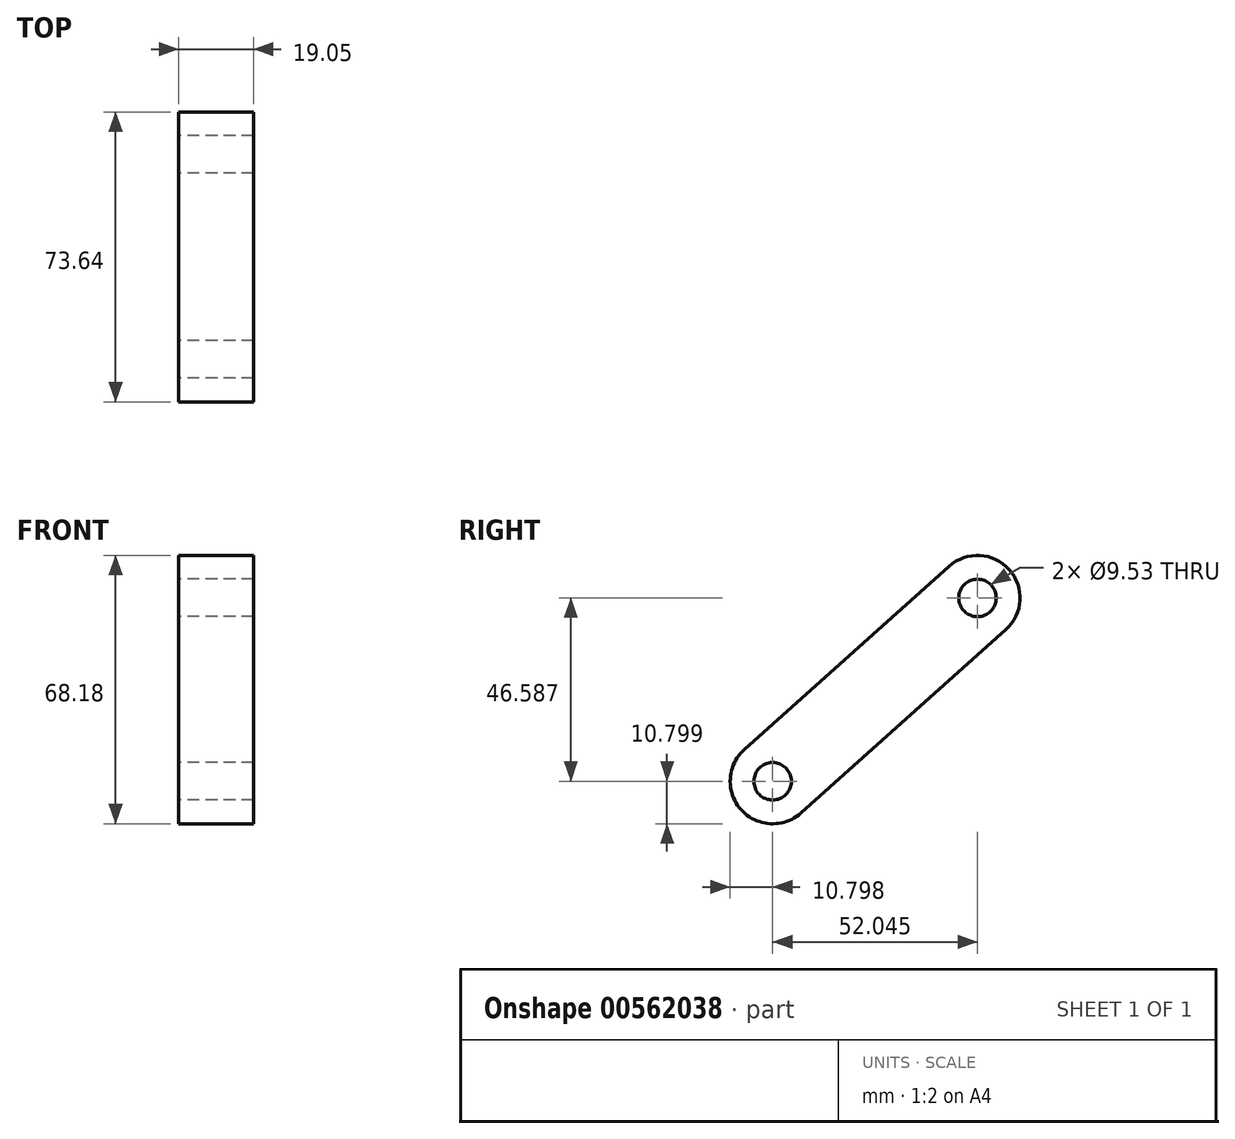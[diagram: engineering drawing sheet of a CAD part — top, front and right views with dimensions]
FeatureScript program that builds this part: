
annotation { "Feature Type Name" : "Feature", "Feature Type Description" : "" }
export const myFeature = defineFeature(function(context is Context, id is Id, definition is map)
    precondition{}
    {
        {
            var Q0;
            Q0=qCreatedBy(makeId("Right.planeOp"),FACE);
            var sketch = newSketch(context, id + "F0", { "sketchPlane" : qUnion([Q0])});
            skLineSegment(sketch, "E0", {"start": v(-513.86, 319.86) * mm, "end": v(-513.86, 78.56) * mm});
            skSolve(sketch);
        }
        {
            var Q0;
            Q0=qCreatedBy(makeId("Right.planeOp"),FACE);
            var sketch = newSketch(context, id + "F1", { "sketchPlane" : qUnion([Q0])});
            skLineSegment(sketch, "E1", {"start": v(-749.75, 255.82) * mm, "end": v(-601.81, 261.03) * mm});
            skLineSegment(sketch, "E2", {"start": v(-562.01, 653.81) * mm, "end": v(-601.81, 261.03) * mm});
            skLineSegment(sketch, "E3", {"start": v(-562.01, 653.81) * mm, "end": v(-749.75, 255.82) * mm});
            skLineSegment(sketch, "E4", {"start": v(-712.77, 291.22) * mm, "end": v(-724.6, 436.35) * mm});
            skLineSegment(sketch, "E5", {"start": v(-712.77, 291.22) * mm, "end": v(-827.72, 541.93) * mm});
            skLineSegment(sketch, "E6", {"start": v(-724.6, 436.35) * mm, "end": v(-827.72, 541.93) * mm});
            skLineSegment(sketch, "E7", {"start": v(-1010.22, 658.42) * mm, "end": v(-827.72, 541.93) * mm});
            skLineSegment(sketch, "E8", {"start": v(-1039.51, 675.34) * mm, "end": v(-1010.22, 658.42) * mm});
            skLineSegment(sketch, "E9", {"start": v(-1039.51, 675.34) * mm, "end": v(-712.77, 291.22) * mm});
            skLineSegment(sketch, "E10", {"start": v(-1010.22, 658.42) * mm, "end": v(-712.77, 291.22) * mm});
            skLineSegment(sketch, "E11", {"start": v(-601.81, 261.03) * mm, "end": v(-595.89, 401.8) * mm});
            skLineSegment(sketch, "E12", {"start": v(-601.81, 261.03) * mm, "end": v(-609.7, 655.84) * mm});
            skLineSegment(sketch, "E13", {"start": v(-595.89, 401.8) * mm, "end": v(-609.7, 655.84) * mm});
            skLineSegment(sketch, "E14", {"start": v(-724.6, 436.35) * mm, "end": v(-595.89, 401.8) * mm});
            skLineSegment(sketch, "E15", {"start": v(-827.72, 541.93) * mm, "end": v(-776.2, 589.57) * mm});
            skLineSegment(sketch, "E16", {"start": v(-749.75, 255.82) * mm, "end": v(-776.2, 589.57) * mm});
            skLineSegment(sketch, "E17", {"start": v(-1043.9, 791.38) * mm, "end": v(-776.2, 589.57) * mm});
            skLineSegment(sketch, "E18", {"start": v(-1392.46, 315.43) * mm, "end": v(-1338.48, 358.4) * mm});
            skLineSegment(sketch, "E19", {"start": v(-1338.48, 358.4) * mm, "end": v(-1296.78, 299.05) * mm});
            skLineSegment(sketch, "E20", {"start": v(-1043.9, 791.38) * mm, "end": v(-1296.78, 299.05) * mm});
            skLineSegment(sketch, "E21", {"start": v(-1296.78, 299.05) * mm, "end": v(-1039.51, 675.34) * mm});
            skLineSegment(sketch, "E22", {"start": v(-1039.51, 675.34) * mm, "end": v(-1043.9, 791.38) * mm});
            skLineSegment(sketch, "E23", {"start": v(-1010.22, 658.42) * mm, "end": v(-1338.48, 358.4) * mm});
            skLineSegment(sketch, "E24", {"start": v(-1392.46, 315.43) * mm, "end": v(-1296.78, 299.05) * mm});
            skLineSegment(sketch, "E25", {"start": v(-1296.78, 299.05) * mm, "end": v(-1296.78, 190.05) * mm});
            skLineSegment(sketch, "E26", {"start": v(-1296.78, 190.05) * mm, "end": v(-1404.89, 208.55) * mm});
            skLineSegment(sketch, "E27", {"start": v(-1404.89, 208.55) * mm, "end": v(-1392.46, 315.43) * mm});
            skLineSegment(sketch, "E28", {"start": v(-1392.46, 315.43) * mm, "end": v(-1296.78, 190.05) * mm});
            skLineSegment(sketch, "E29", {"start": v(0, 0) * mm, "end": v(0, 674.17) * mm});
            skLineSegment(sketch, "E30", {"start": v(-316.61, 320.6) * mm, "end": v(-316.61, 307.94) * mm});
            skLineSegment(sketch, "E31", {"start": v(-400.45, 218.07) * mm, "end": v(-378.01, 218.07) * mm});
            skLineSegment(sketch, "E32", {"start": v(-472.6, 74.76) * mm, "end": v(-472.6, 54.94) * mm});
            skSolve(sketch);
        }
        {
            var Q0;
            Q0=qCreatedBy(makeId("Right.planeOp"),FACE);
            var sketch = newSketch(context, id + "F2", { "sketchPlane" : qUnion([Q0])});
            skArc(sketch, "E33", {"start": v(-782.88, 596.56) * mm, "mid": v(-767.63, 595.72) * mm, "end": v(-768.48, 580.47) * mm});
            skArc(sketch, "E34", {"start": v(-834.92, 549.97) * mm, "mid": v(-835.76, 534.73) * mm, "end": v(-820.52, 533.89) * mm});
            skLineSegment(sketch, "E35", {"start": v(-834.92, 549.97) * mm, "end": v(-782.88, 596.56) * mm});
            skLineSegment(sketch, "E36", {"start": v(-768.48, 580.47) * mm, "end": v(-820.52, 533.89) * mm});
            skCircle(sketch, "E37", {"center": v(-775.68, 588.52) * mm, "radius": 4.76 * mm});
            skCircle(sketch, "E38", {"center": v(-827.72, 541.93) * mm, "radius": 4.76 * mm});
            skSolve(sketch);
        }
        {
            var Q0;
            Q0=qSketchRegion(id+"F2",true);
            extrude(context, id + "F3", {"entities" : qUnion([Q0]), "depth" : 19.05 * mm, "offsetDistance" : 25.4 * mm});
        }
    });
